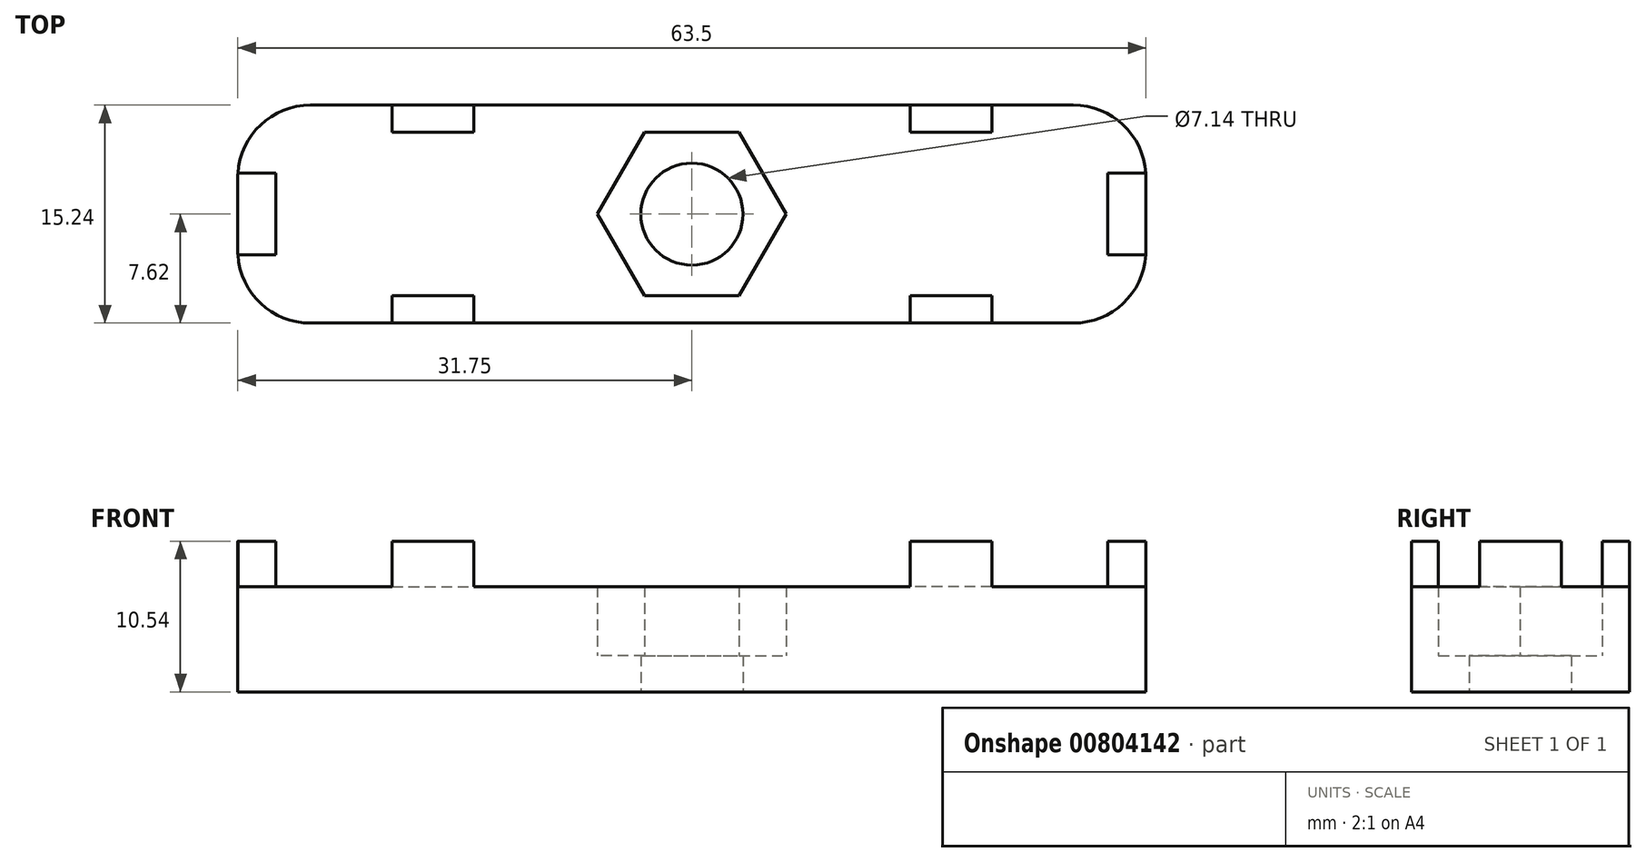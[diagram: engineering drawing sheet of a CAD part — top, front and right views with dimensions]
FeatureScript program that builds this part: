
annotation { "Feature Type Name" : "Feature", "Feature Type Description" : "" }
export const myFeature = defineFeature(function(context is Context, id is Id, definition is map)
    precondition{}
    {
        {
            var Q0;
            Q0=qCreatedBy(makeId("Top.planeOp"),FACE);
            var sketch = newSketch(context, id + "F0", { "sketchPlane" : qUnion([Q0])});
            skLineSegment(sketch, "E0", {"start": v(0, 0) * mm, "end": v(0, 21.76) * mm, "construction": true});
            skLineSegment(sketch, "E1", {"start": v(0, 0) * mm, "end": v(22.94, 0) * mm, "construction": true});
            skLineSegment(sketch, "E2.bottom", {"start": v(-31.75, 7.62) * mm, "end": v(31.75, 7.62) * mm});
            skLineSegment(sketch, "E2.top", {"start": v(-31.75, -7.62) * mm, "end": v(31.75, -7.62) * mm});
            skLineSegment(sketch, "E2.left", {"start": v(-31.75, 7.62) * mm, "end": v(-31.75, -7.62) * mm});
            skLineSegment(sketch, "E2.right", {"start": v(31.75, 7.62) * mm, "end": v(31.75, -7.62) * mm});
            skCircle(sketch, "E3.cCircle", {"center": v(0, 0) * mm, "radius": 5.72 * mm, "construction": true});
            skLineSegment(sketch, "E3.0", {"start": v(-6.6, 0) * mm, "end": v(-3.3, 5.72) * mm});
            skLineSegment(sketch, "E3.1", {"start": v(-3.3, 5.72) * mm, "end": v(3.3, 5.72) * mm});
            skLineSegment(sketch, "E3.2", {"start": v(3.3, 5.72) * mm, "end": v(6.6, 0) * mm});
            skLineSegment(sketch, "E3.3", {"start": v(6.6, 0) * mm, "end": v(3.3, -5.72) * mm});
            skLineSegment(sketch, "E3.4", {"start": v(3.3, -5.72) * mm, "end": v(-3.3, -5.72) * mm});
            skLineSegment(sketch, "E3.5", {"start": v(-3.3, -5.71) * mm, "end": v(-6.6, 0) * mm});
            skPoint(sketch, "E3.0.midPoint", {"position": v(-4.95, 2.86) * mm});
            skSolve(sketch);
        }
        {
            var Q0;
            Q0 = qSketchRegion(id + "F0", true);
            extrude(context, id + "F1", {"entities" : qUnion([Q0]), "depth" : 4.83 * mm, "offsetDistance" : 25.4 * mm});
        }
        {
            var Q0;
            Q0=makeQuery(id+"F1.opExtrude","CAP_FACE",FACE,{"disambiguationData":[OSD([sQuery(id+"F0.wireOp",EDGE,"E2.bottom"),sQuery(id+"F0.wireOp",EDGE,"E2.top"),sQuery(id+"F0.wireOp",EDGE,"E2.left"),sQuery(id+"F0.wireOp",EDGE,"E2.right"),sQuery(id+"F0.wireOp",EDGE,"E3.0"),sQuery(id+"F0.wireOp",EDGE,"E3.1"),sQuery(id+"F0.wireOp",EDGE,"E3.2"),sQuery(id+"F0.wireOp",EDGE,"E3.3"),sQuery(id+"F0.wireOp",EDGE,"E3.4"),sQuery(id+"F0.wireOp",EDGE,"E3.5")])],"isStart":false});
            var sketch = newSketch(context, id + "F2", { "sketchPlane" : qUnion([Q0])});
            skLineSegment(sketch, "E4.bottom", {"start": v(-31.75, -2.86) * mm, "end": v(-29.08, -2.86) * mm});
            skLineSegment(sketch, "E4.top", {"start": v(-31.75, 2.86) * mm, "end": v(-29.08, 2.86) * mm});
            skLineSegment(sketch, "E4.left", {"start": v(-31.75, -2.86) * mm, "end": v(-31.75, 2.86) * mm});
            skLineSegment(sketch, "E4.right", {"start": v(-29.08, -2.86) * mm, "end": v(-29.08, 2.86) * mm});
            skLineSegment(sketch, "E5.bottom", {"start": v(-20.97, -7.62) * mm, "end": v(-15.25, -7.62) * mm});
            skLineSegment(sketch, "E5.top", {"start": v(-20.97, -5.71) * mm, "end": v(-15.25, -5.71) * mm});
            skLineSegment(sketch, "E5.left", {"start": v(-20.97, -7.62) * mm, "end": v(-20.97, -5.71) * mm});
            skLineSegment(sketch, "E5.right", {"start": v(-15.25, -7.62) * mm, "end": v(-15.25, -5.72) * mm});
            skLineSegment(sketch, "E6.MirrorCS", {"start": v(15.25, -7.62) * mm, "end": v(15.25, -5.72) * mm});
            skLineSegment(sketch, "E7.MirrorCS", {"start": v(20.97, -7.62) * mm, "end": v(15.25, -7.62) * mm});
            skLineSegment(sketch, "E8.MirrorCS", {"start": v(20.97, -5.71) * mm, "end": v(15.25, -5.71) * mm});
            skLineSegment(sketch, "E9.MirrorCS", {"start": v(20.97, -7.62) * mm, "end": v(20.97, -5.71) * mm});
            skLineSegment(sketch, "E10.MirrorCS", {"start": v(-20.97, 5.71) * mm, "end": v(-15.25, 5.71) * mm});
            skLineSegment(sketch, "E11.MirrorCS", {"start": v(-20.97, 7.62) * mm, "end": v(-20.97, 5.71) * mm});
            skLineSegment(sketch, "E12.MirrorCS", {"start": v(-20.97, 7.62) * mm, "end": v(-15.25, 7.62) * mm});
            skLineSegment(sketch, "E13.MirrorCS", {"start": v(-15.25, 7.62) * mm, "end": v(-15.25, 5.72) * mm});
            skLineSegment(sketch, "E14.MirrorCS", {"start": v(15.25, 7.62) * mm, "end": v(15.25, 5.72) * mm});
            skLineSegment(sketch, "E15.MirrorCS", {"start": v(20.97, 7.62) * mm, "end": v(15.25, 7.62) * mm});
            skLineSegment(sketch, "E16.MirrorCS", {"start": v(20.97, 5.71) * mm, "end": v(15.25, 5.71) * mm});
            skLineSegment(sketch, "E17.MirrorCS", {"start": v(20.97, 7.62) * mm, "end": v(20.97, 5.71) * mm});
            skLineSegment(sketch, "E18.MirrorCS", {"start": v(31.75, -2.86) * mm, "end": v(29.08, -2.86) * mm});
            skLineSegment(sketch, "E19.MirrorCS", {"start": v(31.75, -2.86) * mm, "end": v(31.75, 2.86) * mm});
            skLineSegment(sketch, "E20.MirrorCS", {"start": v(29.08, -2.86) * mm, "end": v(29.08, 2.86) * mm});
            skLineSegment(sketch, "E21.MirrorCS", {"start": v(31.75, 2.86) * mm, "end": v(29.08, 2.86) * mm});
            skSolve(sketch);
        }
        {
            var Q0;
            Q0 = qSketchRegion(id + "F2", true);
            extrude(context, id + "F3", {"entities" : qUnion([Q0]), "operationType" : NewBodyOperationType.ADD, "depth" : 3.17 * mm, "offsetDistance" : 25.4 * mm});
        }
        {
            var Q0;
            Q0=makeQuery(id+"F1.opExtrude","CAP_FACE",FACE,{"disambiguationData":[OSD([sQuery(id+"F0.wireOp",EDGE,"E2.bottom"),sQuery(id+"F0.wireOp",EDGE,"E2.top"),sQuery(id+"F0.wireOp",EDGE,"E2.left"),sQuery(id+"F0.wireOp",EDGE,"E2.right"),sQuery(id+"F0.wireOp",EDGE,"E3.0"),sQuery(id+"F0.wireOp",EDGE,"E3.1"),sQuery(id+"F0.wireOp",EDGE,"E3.2"),sQuery(id+"F0.wireOp",EDGE,"E3.3"),sQuery(id+"F0.wireOp",EDGE,"E3.4"),sQuery(id+"F0.wireOp",EDGE,"E3.5")])],"isStart":true});
            var sketch = newSketch(context, id + "F4", { "sketchPlane" : qUnion([Q0])});
            skLineSegment(sketch, "E22.bottom", {"start": v(-31.75, 7.62) * mm, "end": v(31.75, 7.62) * mm});
            skLineSegment(sketch, "E22.top", {"start": v(-31.75, -7.62) * mm, "end": v(31.75, -7.62) * mm});
            skLineSegment(sketch, "E22.left", {"start": v(-31.75, 7.62) * mm, "end": v(-31.75, -7.62) * mm});
            skLineSegment(sketch, "E22.right", {"start": v(31.75, 7.62) * mm, "end": v(31.75, -7.62) * mm});
            skPoint(sketch, "E23", {"position": v(0, 0) * mm});
            skSolve(sketch);
        }
        {
            var Q0;
            Q0 = qSketchRegion(id + "F4", true);
            extrude(context, id + "F5", {"entities" : qUnion([Q0]), "operationType" : NewBodyOperationType.ADD, "depth" : 2.54 * mm, "offsetDistance" : 25.4 * mm});
        }
        {
            var Q0;
            Q0=makeQuery(id+"F5.opExtrude","CAP_FACE",FACE,{"disambiguationData":[OSD([sQuery(id+"F4.wireOp",EDGE,"E22.bottom"),sQuery(id+"F4.wireOp",EDGE,"E22.top"),sQuery(id+"F4.wireOp",EDGE,"E22.left"),sQuery(id+"F4.wireOp",EDGE,"E22.right")])],"isStart":false});
            var sketch = newSketch(context, id + "F6", { "sketchPlane" : qUnion([Q0])});
            skPoint(sketch, "E24", {"position": v(0, 0) * mm});
            skSolve(sketch);
        }
        {
            var Q0;
            Q0=sQuery(id+"F6.wireOp",VERTEX,"E24");
            var Q1;
            Q1=makeQuery(id+"F1.opExtrude","SWEPT_BODY",BODY,{"disambiguationData":[OSD([sQuery(id+"F0.wireOp",EDGE,"E2.bottom"),sQuery(id+"F0.wireOp",EDGE,"E2.top"),sQuery(id+"F0.wireOp",EDGE,"E2.left"),sQuery(id+"F0.wireOp",EDGE,"E2.right"),sQuery(id+"F0.wireOp",EDGE,"E3.0"),sQuery(id+"F0.wireOp",EDGE,"E3.1"),sQuery(id+"F0.wireOp",EDGE,"E3.2"),sQuery(id+"F0.wireOp",EDGE,"E3.3"),sQuery(id+"F0.wireOp",EDGE,"E3.4"),sQuery(id+"F0.wireOp",EDGE,"E3.5")])]});
            hole(context, id + "F7", {"style" : HoleStyle.SIMPLE, "endStyle" : HoleEndStyle.THROUGH, "standardTappedOrClearance" : lookupTablePath({ "fit" : "Normal (ASME)", "standard" : "ANSI", "size" : "1/4", "type" : "Clearance" }), "standardBlindInLast" : lookupTablePath({ "fit" : "Normal (ASME)", "standard" : "ANSI", "engagement" : "75%", "pitch" : "20 tpi", "size" : "1/4", "type" : "Clearance & tapped" }), "holeDiameter" : 7.14 * mm, "majorDiameter" : 6.35 * mm, "tappedDepth" : 9.52 * mm, "tapClearance" : 3, "startFromSketch" : true, "locations" : qUnion([Q0]), "scope" : qUnion([Q1])});
        }
        {
            var Q0;
            Q0=makeQuery(id+"F5.boolean.opBoolean","MERGE",EDGE,{"derivedFrom":[makeQuery(id+"F1.opExtrude","SWEPT_EDGE",EDGE,{"disambiguationData":[OSD([sQuery(id+"F0.wireOp",EDGE,"E2.top"),sQuery(id+"F0.wireOp",EDGE,"E2.right")])]}),makeQuery(id+"F5.opExtrude","SWEPT_EDGE",EDGE,{"disambiguationData":[OSD([sQuery(id+"F4.wireOp",EDGE,"E22.bottom"),sQuery(id+"F4.wireOp",EDGE,"E22.right")])]})]});
            var Q1;
            Q1=makeQuery(id+"F5.boolean.opBoolean","MERGE",EDGE,{"derivedFrom":[makeQuery(id+"F1.opExtrude","SWEPT_EDGE",EDGE,{"disambiguationData":[OSD([sQuery(id+"F0.wireOp",EDGE,"E2.bottom"),sQuery(id+"F0.wireOp",EDGE,"E2.right")])]}),makeQuery(id+"F5.opExtrude","SWEPT_EDGE",EDGE,{"disambiguationData":[OSD([sQuery(id+"F4.wireOp",EDGE,"E22.top"),sQuery(id+"F4.wireOp",EDGE,"E22.right")])]})]});
            var Q2;
            Q2=makeQuery(id+"F5.boolean.opBoolean","MERGE",EDGE,{"derivedFrom":[makeQuery(id+"F1.opExtrude","SWEPT_EDGE",EDGE,{"disambiguationData":[OSD([sQuery(id+"F0.wireOp",EDGE,"E2.bottom"),sQuery(id+"F0.wireOp",EDGE,"E2.left")])]}),makeQuery(id+"F5.opExtrude","SWEPT_EDGE",EDGE,{"disambiguationData":[OSD([sQuery(id+"F4.wireOp",EDGE,"E22.top"),sQuery(id+"F4.wireOp",EDGE,"E22.left")])]})]});
            var Q3;
            Q3=makeQuery(id+"F5.boolean.opBoolean","MERGE",EDGE,{"derivedFrom":[makeQuery(id+"F1.opExtrude","SWEPT_EDGE",EDGE,{"disambiguationData":[OSD([sQuery(id+"F0.wireOp",EDGE,"E2.top"),sQuery(id+"F0.wireOp",EDGE,"E2.left")])]}),makeQuery(id+"F5.opExtrude","SWEPT_EDGE",EDGE,{"disambiguationData":[OSD([sQuery(id+"F4.wireOp",EDGE,"E22.bottom"),sQuery(id+"F4.wireOp",EDGE,"E22.left")])]})]});
            fillet(context, id + "F8", {"entities" : qUnion([Q0, Q1, Q2, Q3]), "tangentPropagation" : true, "radius" : 5.08 * mm, "defaultsChanged" : false, "vertexSettings" : [], "allowEdgeOverflow" : false});
        }
    });
